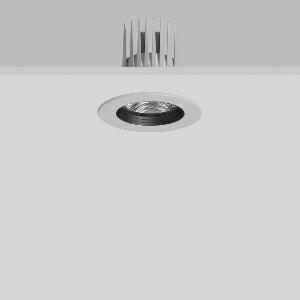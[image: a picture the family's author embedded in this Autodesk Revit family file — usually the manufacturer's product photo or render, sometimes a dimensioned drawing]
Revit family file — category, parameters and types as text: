
# Revit family: heledon_mini_e_901749_004_2_76_0ae5
name_source: partatom
category: Lighting Fixtures
units: mm (PartAtom-declared; Revit-internal decimal feet)

## family parameters
Cut with Voids When Loaded = No
Host = Face
Light Source = No
Part Type = Normal
Room Calculation Point = No
Round Connector Dimension = Use Diameter
Shared = No

## types (1)
- HELEDON mini E (1 x LED Modul 927, 3300 lm, 2700)
    Apparent Load = 29 VA
    Approval mark = CE
    CIE Flux Codes = 99 100 100 100 100
    Color Rendering = 92
    Color Temperature = 2700
    Default Elevation = 1800 mm
    Description = Series: HELEDON mini
Round recessed downlight. Housing: die-cast aluminium, powder-coated. Black plastic ring and recessed LED to prevent glare from the side. Optical assembly with reflector made of MIRO-Silver with 98% total light reflection for outstanding efficiency - can be changed without tools. Best colour rendering index Ra>90. Suitable for Recessed ceiling mounting. Installation without tools thanks to spring fastening system. Including separate LED converter with connecting cable 600 mm.High quality converter without flickering and stroboscopic effect. Through-wiring box (5 pole) available as accessory. The following accessories can be mounted without use of tools: interchangeable lenses, decorative glasses, honeycomb louvre, clear and frosted diffusers, white interchangeable plastic ring. 
Colour: silver
Diameter: 124 mm
Height: 3 mm
Cut-out diameter: 114 mm
Recess height: 170 mm
Luminaire: recess height: 120 mm
Lamp: LED
Socket: without socket
Colour temperature: 2700K
Colour rendering index (CRI): 92
System power: 29 W
Rated luminous flux: 3300 lm
Luminous efficiency: 114 lm/W
Control gear: Converter, dimmable, DALI
Protection class: II
Type of protection: IP 20
    Height = 0 mm  [stored 0 ft]
    Lamp = 1 x LED Modul 927
    Lamp Light Flux = 3300 lm
    Lamp count = 1
    Length = 124 mm  [stored 0.406824 ft]
    Lifetime = 50000 h
    Luminous efficacy = 114 lm/W
    Manufacturer = RZB
    ModVariant = No
    Model = 901749.004.2.76
    Mounting Place = Ceiling
    Mounting Type = Recessed
    Number of Poles = 1
    OnlyDefault = Yes
    Power Factor = 1
    Product Name = HELEDON mini E
    Product group = Recessed downlights
    ProductGroupID = 402
    Protection Class = Protection class II
    Protection Degree = IP 20
    RLX_Detail_Level = 1
    RLX_Emergency_Light_Flux = 0 lm
    RLX_Emergency_Type = 0
    RLX_Emergency_Type_DB = No
    RlxData = <blob elided: 124253 chars, md5=55c00f09>
    Socket = socket
    Standby Power = 0 W
    System Light Flux = 3300 lm
    System Power = 29 W
    Type Comments = Product without accessories
    Type Image = 901657.004.jpg
    URL = http://relux.com
    VarID = ---
    Voltage = 230 V
    Voltage Range = 220-240 V
    Weight = 0.00 kg
    Width = 0 mm  [stored 0 ft]

note: [stored X ft] marks values corroborated as IEEE doubles in the binary element streams (Revit-internal decimal feet)

## geometry (parser evidence)
native form markers: Blend x4, Sweep x11
no freeform markers — native parametric forms only
